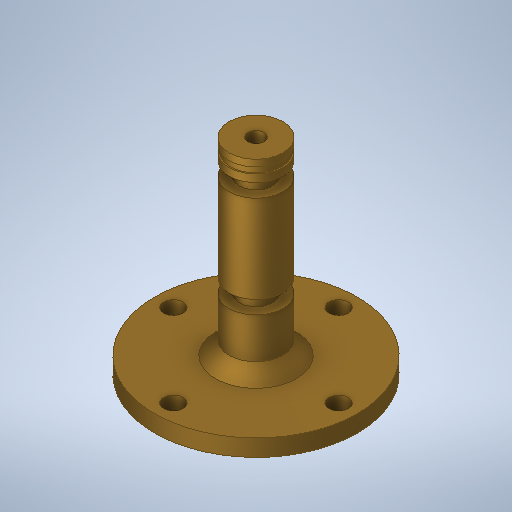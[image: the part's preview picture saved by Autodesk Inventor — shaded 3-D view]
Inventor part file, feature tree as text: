
AUTODESK INVENTOR PART (.ipt)
format: ipt  version: 2025 (Build 290162000, 162)  size: 343,040 bytes
history: native  units: in
note: dims shown in document units (in); Inventor stores cm internally (conversion verified against a paired STEP export)
features: extrude x4, sketch x2, chamfer x1, revolve x1, hole x1
ambient origin geometry x8: Origin, YZ Plane, XZ Plane, XY Plane, X Axis, Y Axis, Z Axis, Center Point
bodies: Solid1 (feature_tree)
feature tree (9):
  extrude  "Extrusion1"  Depth=0.0984in TaperAngle=0.0deg
  extrude  "Extrusion2"  Depth=0.0787in
  extrude  "Extrusion3"  Depth=0.0512in TaperAngle=0.0deg
  extrude  "Extrusion4"  Depth=0.315in
  chamfer  "Chamfer1"  Distance=1.1024in
  revolve  "Revolution1"  [1 undecoded]
  hole  "Hole1"  [1 undecoded]
  sketch  "Sketch6"  dims[d3=0.3425in d4=0.1614in d5=0.0512in d6=0.0in d7=0.315in d8=1.1024in d9=0.0in d10=0.0945in d11=1.107in d12=0.0in d13=0.0787in d14=0.125in d15=45.0deg d16=0.0394in d17=0.0354in d18=0.0079in d19=0.1181in d20=0.0787in d21=0.0591in d22=0.7087in d23=0.0787in d24=90.0deg d25=0.9646in d33=1.5748in d35=360.0deg d37=0.1142in d38=0.1969in d39=0.2165in d40=0.0787in d41=90.0deg d42=0.2362in d43=0.8108in]
  sketch  "Sketch Circular Pattern2"  dims[d0=1.1811in d1=0.0984in d2=0.0in]
note: 2 required parameter values undecoded (feature->parameter linkage not recoverable at this tier; creation-order binding heuristic only, values carry confidence <= 0.55)